# Revit family: Commercial-Kitchen-Vent
name_source: partatom
category: Mechanical Equipment
units: mm (PartAtom-declared; Revit-internal decimal feet)

## family parameters
Always vertical = Yes
Classification Number = 23.40.40.14.21
Cut with Voids When Loaded = No
Host = Ceiling
Maintain Annotation Orientation = No
Part Type = Normal
Room Calculation Point = No
Round Connector Dimension = Use Diameter
Shared = No

## types (6) — shared parameters
Body Material = ARCAT - Metal - Steel_Stainless
Compliance = UL710, NSF
Construction Details = http://www.arcat.com
Default Elevation = 0' - 0"
Depth = 4' - 0"
Expected Lifespan (Years) = 10
Fin Material = ARCAT - Metal - Aluminum_Black
Green Building-LEED = http://www.arcat.com
Height = 5' - 0"
Keynote = 11425
Maintenance Schedule (Months) = 3
Manufacturer = Generic
Manufacturer Fax = (203) 929-2444
Manufacturer Website = http://www.arcat.com
Model = Generic
Product Data = http://www.arcat.com
Product Properties = http://www.arcat.com
Specification = http://www.arcat.com
URL = http://www.arcat.com
Warranty Duration (Years) = 1

## per-type parameters (varying)
| type | Assembly Code | Description | Flow Rate_Lf |
| 300cfm |  | Medium-Duty Canopy Commercial Kitchen Vent (CKV) | 300 |
| 150cfm |  | Light-Duty Canopy Commercial Kitchen Vent (CKV) | 150 |
| 250cfm | D3040200 | Medium-Duty Canopy Commercial Kitchen Vent (CKV) | 250 |
| 200cfm |  | Light-Duty Canopy Commercial Kitchen Vent (CKV) | 200 |
| 350cfm |  | Heavy-Duty Canopy Commercial Kitchen Vent (CKV) | 350 |
| 400cfm |  | Extra-Heavy-Duty Canopy Commercial Kitchen Vent (CKV) | 400 |

## geometry (parser evidence)
native form markers: Sweep x3
no freeform markers — native parametric forms only
